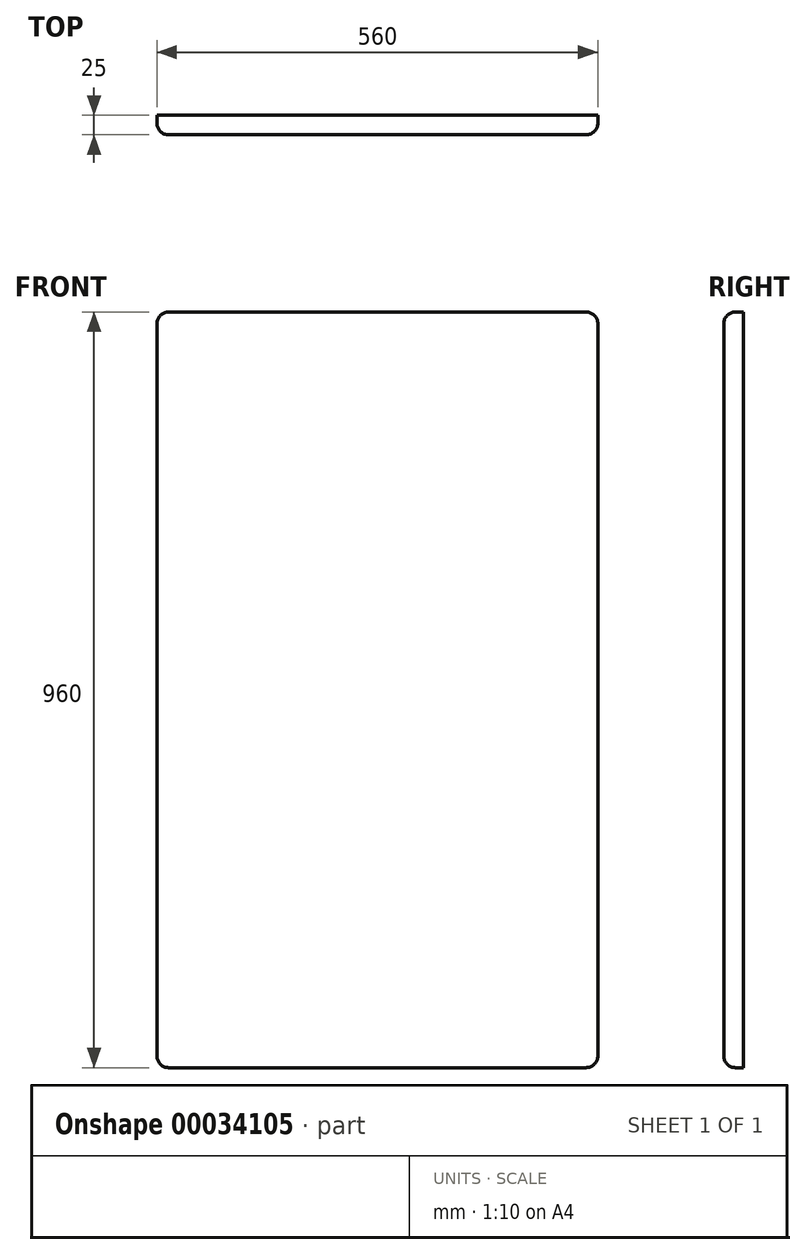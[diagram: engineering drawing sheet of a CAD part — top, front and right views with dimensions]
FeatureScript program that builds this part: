
annotation { "Feature Type Name" : "Feature", "Feature Type Description" : "" }
export const myFeature = defineFeature(function(context is Context, id is Id, definition is map)
    precondition{}
    {
        {
            var Q0;
            Q0=qCreatedBy(makeId("Front.planeOp"),FACE);
            var sketch = newSketch(context, id + "F0", { "sketchPlane" : qUnion([Q0])});
            skLineSegment(sketch, "E0.bottom", {"start": v(-280, 480) * mm, "end": v(280, 480) * mm});
            skLineSegment(sketch, "E0.top", {"start": v(-280, -480) * mm, "end": v(280, -480) * mm});
            skLineSegment(sketch, "E0.left", {"start": v(-280, 480) * mm, "end": v(-280, -480) * mm});
            skLineSegment(sketch, "E0.right", {"start": v(280, 480) * mm, "end": v(280, -480) * mm});
            skLineSegment(sketch, "E1", {"start": v(0, 480) * mm, "end": v(0, -480) * mm, "construction": true});
            skLineSegment(sketch, "E2", {"start": v(-280, 0) * mm, "end": v(280, 0) * mm, "construction": true});
            skLineSegment(sketch, "E3.rect.bottom", {"start": v(245, 445) * mm, "end": v(-245, 445) * mm, "construction": true});
            skLineSegment(sketch, "E3.rect.top", {"start": v(245, -445) * mm, "end": v(-245, -445) * mm, "construction": true});
            skLineSegment(sketch, "E3.rect.left", {"start": v(245, 445) * mm, "end": v(245, -445) * mm, "construction": true});
            skLineSegment(sketch, "E3.rect.right", {"start": v(-245, 445) * mm, "end": v(-245, -445) * mm, "construction": true});
            skPoint(sketch, "E3.rect.middle", {"position": v(0, 0) * mm});
            skLineSegment(sketch, "E4.rect.bottom", {"start": v(261, 461) * mm, "end": v(-261, 461) * mm, "construction": true});
            skLineSegment(sketch, "E4.rect.top", {"start": v(261, -461) * mm, "end": v(-261, -461) * mm, "construction": true});
            skLineSegment(sketch, "E4.rect.left", {"start": v(261, 461) * mm, "end": v(261, -461) * mm, "construction": true});
            skLineSegment(sketch, "E4.rect.right", {"start": v(-261, 461) * mm, "end": v(-261, -461) * mm, "construction": true});
            skSolve(sketch);
        }
        {
            var Q0;
            Q0=makeQuery(id+"F0.imprint","IMPRINT",FACE,{"disambiguationData":[TD([[makeQuery(id+"F0.imprint","IMPRINT",EDGE,{"derivedFrom":sQuery(id+"F0.wireOp",EDGE,"E0.bottom")}),-1.0]])]});
            var sketch = newSketch(context, id + "F1", { "sketchPlane" : qUnion([Q0])});
            skSolve(sketch);
        }
        {
            var Q0;
            Q0=makeQuery(id+"F0.imprint","IMPRINT",FACE,{"disambiguationData":[TD([[makeQuery(id+"F0.imprint","IMPRINT",EDGE,{"derivedFrom":sQuery(id+"F0.wireOp",EDGE,"E0.bottom")}),-1.0]])]});
            extrude(context, id + "F2", {"entities" : qUnion([Q0]), "oppositeDirection" : true, "depth" : 25 * mm});
        }
        {
            var Q0;
            Q0=makeQuery(id+"F2.opExtrude","CAP_FACE",FACE,{"disambiguationData":[OSD([sQuery(id+"F0.wireOp",EDGE,"E0.bottom"),sQuery(id+"F0.wireOp",EDGE,"E0.top"),sQuery(id+"F0.wireOp",EDGE,"E0.left"),sQuery(id+"F0.wireOp",EDGE,"E0.right")])],"isStart":true});
            fillet(context, id + "F3", {"entities" : qUnion([Q0]), "radius" : 15 * mm, "tangentPropagation" : true, "allowEdgeOverflow" : false});
        }
        {
            var Q0;
            Q0=makeQuery(id+"F3.opFillet","BLEND_EDGE",EDGE,{"blendedFrom":[makeQuery(id+"F2.opExtrude","CAP_EDGE",EDGE,{"disambiguationData":[OSD([sQuery(id+"F0.wireOp",EDGE,"E0.bottom")])],"isStart":true}),makeQuery(id+"F2.opExtrude","CAP_EDGE",EDGE,{"disambiguationData":[OSD([sQuery(id+"F0.wireOp",EDGE,"E0.right")])],"isStart":true})],"blendedInto":[]});
            var Q1;
            Q1=makeQuery(id+"F3.opFillet","BLEND_EDGE",EDGE,{"blendedFrom":[makeQuery(id+"F2.opExtrude","CAP_EDGE",EDGE,{"disambiguationData":[OSD([sQuery(id+"F0.wireOp",EDGE,"E0.bottom")])],"isStart":true}),makeQuery(id+"F2.opExtrude","CAP_EDGE",EDGE,{"disambiguationData":[OSD([sQuery(id+"F0.wireOp",EDGE,"E0.left")])],"isStart":true})],"blendedInto":[]});
            var Q2;
            Q2=makeQuery(id+"F3.opFillet","BLEND_EDGE",EDGE,{"blendedFrom":[makeQuery(id+"F2.opExtrude","CAP_EDGE",EDGE,{"disambiguationData":[OSD([sQuery(id+"F0.wireOp",EDGE,"E0.top")])],"isStart":true}),makeQuery(id+"F2.opExtrude","CAP_EDGE",EDGE,{"disambiguationData":[OSD([sQuery(id+"F0.wireOp",EDGE,"E0.right")])],"isStart":true})],"blendedInto":[]});
            var Q3;
            Q3=makeQuery(id+"F3.opFillet","BLEND_EDGE",EDGE,{"blendedFrom":[makeQuery(id+"F2.opExtrude","CAP_EDGE",EDGE,{"disambiguationData":[OSD([sQuery(id+"F0.wireOp",EDGE,"E0.top")])],"isStart":true}),makeQuery(id+"F2.opExtrude","CAP_EDGE",EDGE,{"disambiguationData":[OSD([sQuery(id+"F0.wireOp",EDGE,"E0.left")])],"isStart":true})],"blendedInto":[]});
            var Q4;
            Q4=makeQuery(id+"F2.opExtrude","CAP_FACE",FACE,{"disambiguationData":[OSD([sQuery(id+"F0.wireOp",EDGE,"E0.bottom"),sQuery(id+"F0.wireOp",EDGE,"E0.top"),sQuery(id+"F0.wireOp",EDGE,"E0.left"),sQuery(id+"F0.wireOp",EDGE,"E0.right")])],"isStart":true});
            fillet(context, id + "F4", {"entities" : qUnion([Q0, Q1, Q2, Q3, Q4]), "radius" : 15 * mm, "tangentPropagation" : true, "allowEdgeOverflow" : false});
        }
    });
